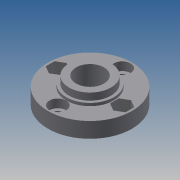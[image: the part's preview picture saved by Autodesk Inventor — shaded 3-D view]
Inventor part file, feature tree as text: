
AUTODESK INVENTOR PART (.ipt)
format: ipt  version: 2013 (Build 170138000, 138)  size: 163,840 bytes
history: native  units: mm
features: extrude x7, sketch x7, pattern_circular x2
ambient origin geometry x8: Origin, YZ Plane, XZ Plane, XY Plane, X Axis, Y Axis, Z Axis, Center Point
bodies: Solid1 (feature_tree)
feature tree (16):
  extrude  "Extrusion1"  Depth=4.5mm TaperAngle=0.0deg
  extrude  "Extrusion2"  Depth=1.0mm TaperAngle=0.0deg
  extrude  "Extrusion3"  Depth=1.0mm TaperAngle=0.0deg
  extrude  "Extrusion4"  Depth=3.5mm
  pattern_circular  "Circular Pattern1"  Count=4 Angle=360.0deg
  extrude  "Extrusion5"  Depth=3.0mm TaperAngle=0.0deg
  extrude  "Extrusion6"  Depth=4.0mm TaperAngle=0.0deg
  pattern_circular  "Circular Pattern2"  Count=2 Angle=360.0deg
  extrude  "Extrusion7"  Depth=10.0mm
  sketch  "Sketch1"  dims[d0=32.0mm d3=4.5mm d4=0.0mm]
  sketch  "Sketch2"  dims[d5=17.0mm d8=1.0mm d9=0.0mm]
  sketch  "Sketch3"  dims[d10=15.0mm d12=1.0mm d13=0.0mm]
  sketch  "Sketch4"  dims[d15=11.5mm d16=3.5mm]
  sketch  "Sketch5"  dims[d17=1.0mm d18=0.0mm d19=40.0mm d20=360.0deg]
  sketch  "Sketch6"  dims[d22=6.0mm d26=3.0mm d27=0.0mm]
  sketch  "Sketch7"  dims[d28=5.5mm d29=4.0mm d30=0.0mm d31=20.0mm d32=360.0deg d34=10.0mm d36=9.0mm d37=0.0mm d40=6.0mm d41=6.0mm]
